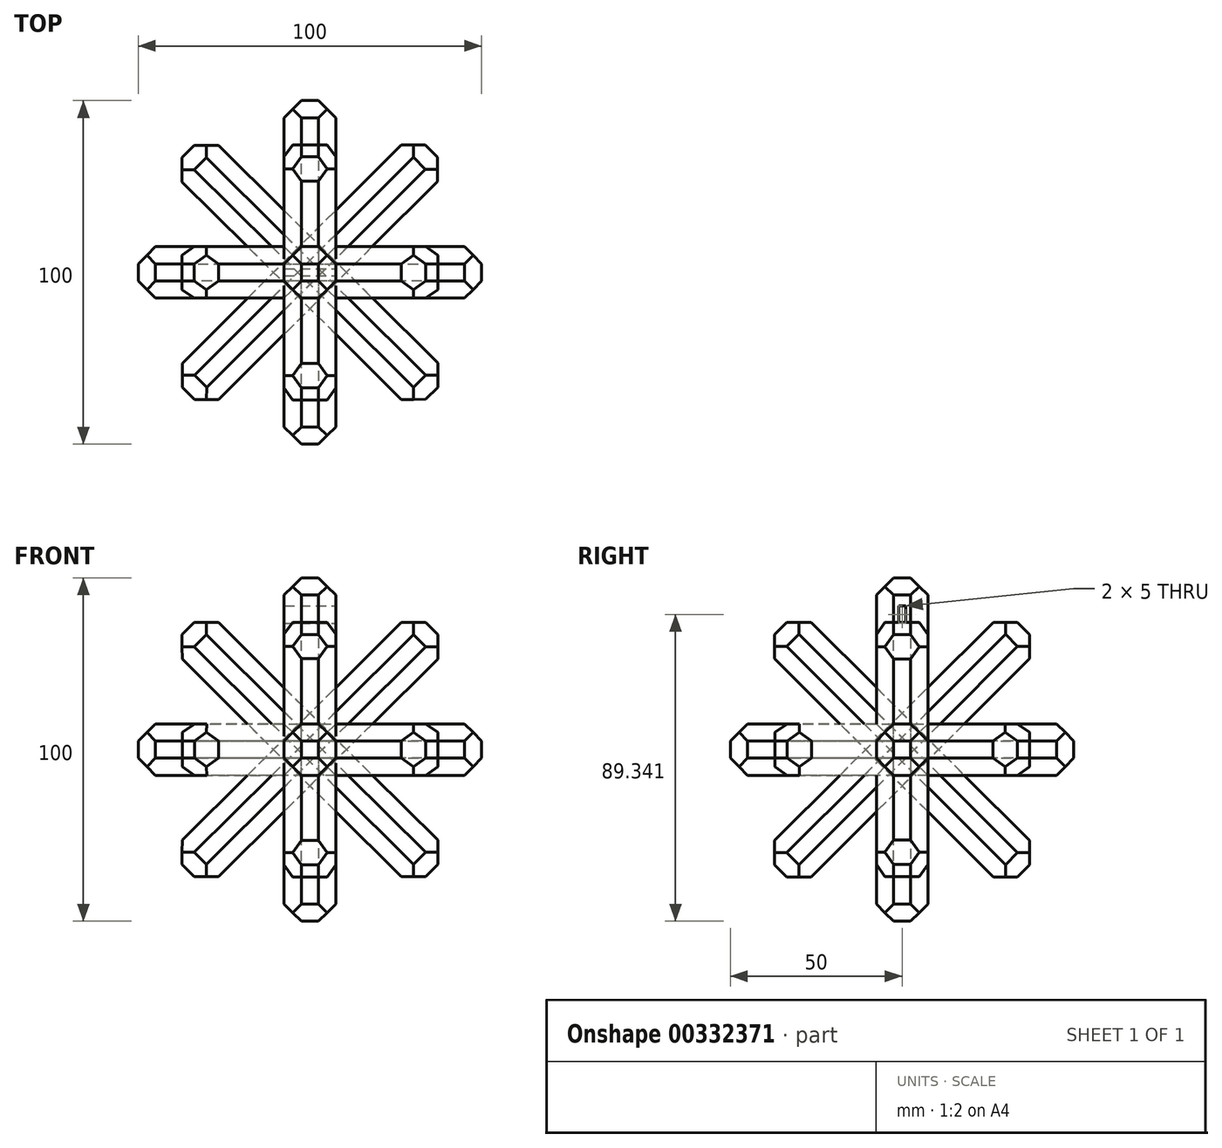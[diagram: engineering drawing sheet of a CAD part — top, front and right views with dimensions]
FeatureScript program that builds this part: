
annotation { "Feature Type Name" : "Feature", "Feature Type Description" : "" }
export const myFeature = defineFeature(function(context is Context, id is Id, definition is map)
    precondition{}
    {
        {
            var Q0;
            Q0=qCreatedBy(makeId("Top.planeOp"),FACE);
            var sketch = newSketch(context, id + "F0", { "sketchPlane" : qUnion([Q0])});
            skLineSegment(sketch, "E0.bottom", {"start": v(50, 7.5) * mm, "end": v(-50, 7.5) * mm});
            skLineSegment(sketch, "E0.top", {"start": v(50, -7.5) * mm, "end": v(-50, -7.5) * mm});
            skLineSegment(sketch, "E0.left", {"start": v(50, 7.5) * mm, "end": v(50, -7.5) * mm});
            skLineSegment(sketch, "E0.right", {"start": v(-50, 7.5) * mm, "end": v(-50, -7.5) * mm});
            skPoint(sketch, "E0.middle", {"position": v(0, 0) * mm});
            skSolve(sketch);
        }
        {
            var Q0;
            Q0=qCreatedBy(makeId("Right.planeOp"),FACE);
            var sketch = newSketch(context, id + "F1", { "sketchPlane" : qUnion([Q0])});
            skLineSegment(sketch, "E1.bottom", {"start": v(50, 7.5) * mm, "end": v(-50, 7.5) * mm});
            skLineSegment(sketch, "E1.top", {"start": v(50, -7.5) * mm, "end": v(-50, -7.5) * mm});
            skLineSegment(sketch, "E1.left", {"start": v(50, 7.5) * mm, "end": v(50, -7.5) * mm});
            skLineSegment(sketch, "E1.right", {"start": v(-50, 7.5) * mm, "end": v(-50, -7.5) * mm});
            skPoint(sketch, "E1.middle", {"position": v(0, 0) * mm});
            skSolve(sketch);
        }
        {
            var Q0;
            Q0 = qSketchRegion(id + "F0", true);
            extrude(context, id + "F2", {"entities" : qUnion([Q0]), "endBound" : BoundingType.SYMMETRIC, "depth" : 15 * mm});
        }
        {
            var Q0;
            Q0=makeQuery(id+"F1.imprint","IMPRINT",FACE,{"disambiguationData":[TD([[makeQuery(id+"F1.imprint","IMPRINT",EDGE,{"derivedFrom":sQuery(id+"F1.wireOp",EDGE,"E1.bottom")}),1.0]])]});
            extrude(context, id + "F3", {"entities" : qUnion([Q0]), "operationType" : NewBodyOperationType.ADD, "endBound" : BoundingType.SYMMETRIC, "depth" : 15 * mm});
        }
        {
            var Q0;
            Q0=qCreatedBy(makeId("Front.planeOp"),FACE);
            var sketch = newSketch(context, id + "F4", { "sketchPlane" : qUnion([Q0])});
            skLineSegment(sketch, "E2.bottom", {"start": v(-7.5, 50) * mm, "end": v(7.5, 50) * mm});
            skLineSegment(sketch, "E2.top", {"start": v(-7.5, -50) * mm, "end": v(7.5, -50) * mm});
            skLineSegment(sketch, "E2.left", {"start": v(-7.5, 50) * mm, "end": v(-7.5, -50) * mm});
            skLineSegment(sketch, "E2.right", {"start": v(7.5, 50) * mm, "end": v(7.5, -50) * mm});
            skPoint(sketch, "E2.middle", {"position": v(0, 0) * mm});
            skSolve(sketch);
        }
        {
            var Q0;
            Q0=makeQuery(id+"F4.imprint","IMPRINT",FACE,{"disambiguationData":[TD([[makeQuery(id+"F4.imprint","IMPRINT",EDGE,{"derivedFrom":sQuery(id+"F4.wireOp",EDGE,"E2.bottom")}),-1.0]])]});
            extrude(context, id + "F5", {"entities" : qUnion([Q0]), "operationType" : NewBodyOperationType.ADD, "endBound" : BoundingType.SYMMETRIC, "depth" : 15 * mm});
        }
        {
            var Q0;
            Q0=qCreatedBy(makeId("Top.planeOp"),FACE);
            var sketch = newSketch(context, id + "F6", { "sketchPlane" : qUnion([Q0])});
            skLineSegment(sketch, "E3.bottom", {"start": v(40.78, -29.9) * mm, "end": v(-30.21, 40.54) * mm});
            skLineSegment(sketch, "E3.top", {"start": v(30.21, -40.54) * mm, "end": v(-40.78, 29.9) * mm});
            skLineSegment(sketch, "E3.left", {"start": v(40.78, -29.9) * mm, "end": v(30.21, -40.54) * mm});
            skLineSegment(sketch, "E3.right", {"start": v(-30.21, 40.54) * mm, "end": v(-40.78, 29.9) * mm});
            skPoint(sketch, "E3.middle", {"position": v(0, 0) * mm});
            skSolve(sketch);
        }
        {
            var Q0;
            Q0=makeQuery(id+"F6.imprint","IMPRINT",FACE,{"disambiguationData":[TD([[makeQuery(id+"F6.imprint","IMPRINT",EDGE,{"derivedFrom":sQuery(id+"F6.wireOp",EDGE,"E3.bottom")}),1.0]])]});
            extrude(context, id + "F7", {"entities" : qUnion([Q0]), "endBound" : BoundingType.SYMMETRIC, "depth" : 15 * mm});
        }
        {
            var Q0;
            Q0=qCreatedBy(makeId("Top.planeOp"),FACE);
            var sketch = newSketch(context, id + "F8", { "sketchPlane" : qUnion([Q0])});
            skLineSegment(sketch, "E4.bottom", {"start": v(30.1, 40.62) * mm, "end": v(-40.7, -30) * mm});
            skLineSegment(sketch, "E4.top", {"start": v(40.7, 30) * mm, "end": v(-30.1, -40.62) * mm});
            skLineSegment(sketch, "E4.left", {"start": v(30.1, 40.62) * mm, "end": v(40.7, 30) * mm});
            skLineSegment(sketch, "E4.right", {"start": v(-40.7, -30) * mm, "end": v(-30.1, -40.62) * mm});
            skPoint(sketch, "E4.middle", {"position": v(0, 0) * mm});
            skSolve(sketch);
        }
        {
            var Q0;
            Q0=makeQuery(id+"F8.imprint","IMPRINT",FACE,{"disambiguationData":[TD([[makeQuery(id+"F8.imprint","IMPRINT",EDGE,{"derivedFrom":sQuery(id+"F8.wireOp",EDGE,"E4.bottom")}),1.0]])]});
            extrude(context, id + "F9", {"entities" : qUnion([Q0]), "endBound" : BoundingType.SYMMETRIC, "depth" : 15 * mm});
        }
        {
            var Q0;
            Q0=qCreatedBy(makeId("Front.planeOp"),FACE);
            var sketch = newSketch(context, id + "F10", { "sketchPlane" : qUnion([Q0])});
            skLineSegment(sketch, "E5.bottom", {"start": v(40.76, -29.9) * mm, "end": v(-30.2, 40.55) * mm});
            skLineSegment(sketch, "E5.top", {"start": v(30.2, -40.55) * mm, "end": v(-40.76, 29.9) * mm});
            skLineSegment(sketch, "E5.left", {"start": v(40.76, -29.9) * mm, "end": v(30.2, -40.55) * mm});
            skLineSegment(sketch, "E5.right", {"start": v(-30.2, 40.55) * mm, "end": v(-40.76, 29.9) * mm});
            skPoint(sketch, "E5.middle", {"position": v(0, 0) * mm});
            skSolve(sketch);
        }
        {
            var Q0;
            Q0=makeQuery(id+"F10.imprint","IMPRINT",FACE,{"disambiguationData":[TD([[makeQuery(id+"F10.imprint","IMPRINT",EDGE,{"derivedFrom":sQuery(id+"F10.wireOp",EDGE,"E5.bottom")}),1.0]])]});
            extrude(context, id + "F11", {"entities" : qUnion([Q0]), "endBound" : BoundingType.SYMMETRIC, "depth" : 15 * mm});
        }
        {
            var Q0;
            Q0=makeQuery(id+"F11.opExtrude","SWEPT_BODY",BODY,{"disambiguationData":[OSD([sQuery(id+"F10.wireOp",EDGE,"E5.bottom"),sQuery(id+"F10.wireOp",EDGE,"E5.top"),sQuery(id+"F10.wireOp",EDGE,"E5.left"),sQuery(id+"F10.wireOp",EDGE,"E5.right")])]});
            var Q1;
            Q1=qCreatedBy(makeId("Right.planeOp"),FACE);
            mirror(context, id + "F12", {"entities" : qUnion([Q0]), "mirrorPlane" : qUnion([Q1])});
        }
        {
            var Q0;
            Q0=qCreatedBy(makeId("Right.planeOp"),FACE);
            var sketch = newSketch(context, id + "F13", { "sketchPlane" : qUnion([Q0])});
            skLineSegment(sketch, "E6.bottom", {"start": v(-30.1, 40.62) * mm, "end": v(40.7, -30) * mm});
            skLineSegment(sketch, "E6.top", {"start": v(-40.7, 30) * mm, "end": v(30.1, -40.62) * mm});
            skLineSegment(sketch, "E6.left", {"start": v(-30.1, 40.62) * mm, "end": v(-40.7, 30) * mm});
            skLineSegment(sketch, "E6.right", {"start": v(40.7, -30) * mm, "end": v(30.1, -40.62) * mm});
            skPoint(sketch, "E6.middle", {"position": v(0, 0) * mm});
            skSolve(sketch);
        }
        {
            var Q0;
            Q0=makeQuery(id+"F13.imprint","IMPRINT",FACE,{"disambiguationData":[TD([[makeQuery(id+"F13.imprint","IMPRINT",EDGE,{"derivedFrom":sQuery(id+"F13.wireOp",EDGE,"E6.bottom")}),-1.0]])]});
            extrude(context, id + "F14", {"entities" : qUnion([Q0]), "endBound" : BoundingType.SYMMETRIC, "depth" : 15 * mm});
        }
        {
            var Q0;
            Q0=makeQuery(id+"F14.opExtrude","SWEPT_BODY",BODY,{"disambiguationData":[OSD([sQuery(id+"F13.wireOp",EDGE,"E6.bottom"),sQuery(id+"F13.wireOp",EDGE,"E6.top"),sQuery(id+"F13.wireOp",EDGE,"E6.left"),sQuery(id+"F13.wireOp",EDGE,"E6.right")])]});
            var Q1;
            Q1=qCreatedBy(makeId("Front.planeOp"),FACE);
            mirror(context, id + "F15", {"entities" : qUnion([Q0]), "mirrorPlane" : qUnion([Q1])});
        }
        {
            var Q0;
            Q0=makeQuery(id+"F14.opExtrude","SWEPT_EDGE",EDGE,{"disambiguationData":[OSD([sQuery(id+"F13.wireOp",EDGE,"E6.top"),sQuery(id+"F13.wireOp",EDGE,"E6.left")])]});
            chamfer(context, id + "F16", {"entities" : qUnion([Q0]), "width" : 5 * mm, "tangentPropagation" : true});
        }
        {
            var Q0;
            Q0=makeQuery(id+"F14.opExtrude","CAP_EDGE",EDGE,{"disambiguationData":[OSD([sQuery(id+"F13.wireOp",EDGE,"E6.left")])],"isStart":false});
            chamfer(context, id + "F17", {"entities" : qUnion([Q0]), "width" : 5 * mm, "tangentPropagation" : true});
        }
        {
            var Q0;
            Q0=makeQuery(id+"F14.opExtrude","SWEPT_EDGE",EDGE,{"disambiguationData":[OSD([sQuery(id+"F13.wireOp",EDGE,"E6.bottom"),sQuery(id+"F13.wireOp",EDGE,"E6.left")])]});
            chamfer(context, id + "F18", {"entities" : qUnion([Q0]), "width" : 5 * mm, "tangentPropagation" : true});
        }
        {
            var Q0;
            Q0=makeQuery(id+"F14.opExtrude","CAP_EDGE",EDGE,{"disambiguationData":[OSD([sQuery(id+"F13.wireOp",EDGE,"E6.left")])],"isStart":true});
            chamfer(context, id + "F19", {"entities" : qUnion([Q0]), "width" : 5 * mm, "tangentPropagation" : true});
        }
        {
            var Q0;
            Q0=makeQuery(id+"F3.opExtrude","SWEPT_EDGE",EDGE,{"disambiguationData":[OSD([sQuery(id+"F1.wireOp",EDGE,"E1.bottom"),sQuery(id+"F1.wireOp",EDGE,"E1.right")])]});
            chamfer(context, id + "F20", {"entities" : qUnion([Q0]), "width" : 5 * mm, "tangentPropagation" : true});
        }
        {
            var Q0;
            Q0=makeQuery(id+"F3.opExtrude","CAP_EDGE",EDGE,{"disambiguationData":[OSD([sQuery(id+"F1.wireOp",EDGE,"E1.right")])],"isStart":false});
            chamfer(context, id + "F21", {"entities" : qUnion([Q0]), "width" : 5 * mm, "tangentPropagation" : true});
        }
        {
            var Q0;
            Q0=makeQuery(id+"F3.opExtrude","CAP_EDGE",EDGE,{"disambiguationData":[OSD([sQuery(id+"F1.wireOp",EDGE,"E1.right")])],"isStart":true});
            chamfer(context, id + "F22", {"entities" : qUnion([Q0]), "width" : 5 * mm, "tangentPropagation" : true});
        }
        {
            var Q0;
            Q0=makeQuery(id+"F3.opExtrude","SWEPT_EDGE",EDGE,{"disambiguationData":[OSD([sQuery(id+"F1.wireOp",EDGE,"E1.top"),sQuery(id+"F1.wireOp",EDGE,"E1.right")])]});
            chamfer(context, id + "F23", {"entities" : qUnion([Q0]), "width" : 5 * mm, "tangentPropagation" : true});
        }
        {
            var Q0;
            {var subQ0=sQuery(id+"F1.wireOp",EDGE,"E1.bottom");var subQ2=sQuery(id+"F0.wireOp",EDGE,"E0.top");Q0=makeQuery(id+"F3.boolean.opBoolean","SPLIT",EDGE,{"disambiguationData":[TD([makeQuery(id+"F2.opExtrude","SWEPT_FACE",FACE,{"disambiguationData":[OSD([subQ2])]})])],"derivedFrom":makeQuery(id+"F3.opExtrude","CAP_EDGE",EDGE,{"disambiguationData":[OSD([subQ0])],"isStart":false})});}
            chamfer(context, id + "F24", {"entities" : qUnion([Q0]), "width" : 5 * mm, "tangentPropagation" : true});
        }
        {
            var Q0;
            {var subQ0=sQuery(id+"F1.wireOp",EDGE,"E1.bottom");var subQ1=sQuery(id+"F0.wireOp",EDGE,"E0.top");Q0=makeQuery(id+"F3.boolean.opBoolean","SPLIT",EDGE,{"disambiguationData":[TD([makeQuery(id+"F2.opExtrude","SWEPT_FACE",FACE,{"disambiguationData":[OSD([subQ1])]})])],"derivedFrom":makeQuery(id+"F3.opExtrude","CAP_EDGE",EDGE,{"disambiguationData":[OSD([subQ0])],"isStart":true})});}
            chamfer(context, id + "F25", {"entities" : qUnion([Q0]), "width" : 5 * mm, "tangentPropagation" : true});
        }
        {
            var Q0;
            {var subQ0=sQuery(id+"F1.wireOp",EDGE,"E1.top");var subQ2=sQuery(id+"F0.wireOp",EDGE,"E0.top");Q0=makeQuery(id+"F3.boolean.opBoolean","SPLIT",EDGE,{"disambiguationData":[TD([makeQuery(id+"F2.opExtrude","SWEPT_FACE",FACE,{"disambiguationData":[OSD([subQ2])]})])],"derivedFrom":makeQuery(id+"F3.opExtrude","CAP_EDGE",EDGE,{"disambiguationData":[OSD([subQ0])],"isStart":false})});}
            chamfer(context, id + "F26", {"entities" : qUnion([Q0]), "width" : 5 * mm, "tangentPropagation" : true});
        }
        {
            var Q0;
            {var subQ0=sQuery(id+"F1.wireOp",EDGE,"E1.top");var subQ2=sQuery(id+"F0.wireOp",EDGE,"E0.top");Q0=makeQuery(id+"F3.boolean.opBoolean","SPLIT",EDGE,{"disambiguationData":[TD([makeQuery(id+"F2.opExtrude","SWEPT_FACE",FACE,{"disambiguationData":[OSD([subQ2])]})])],"derivedFrom":makeQuery(id+"F3.opExtrude","CAP_EDGE",EDGE,{"disambiguationData":[OSD([subQ0])],"isStart":true})});}
            chamfer(context, id + "F27", {"entities" : qUnion([Q0]), "width" : 5 * mm, "tangentPropagation" : true});
        }
        {
            var Q0;
            Q0=makeQuery(id+"F5.opExtrude","SWEPT_EDGE",EDGE,{"disambiguationData":[OSD([sQuery(id+"F4.wireOp",EDGE,"E2.bottom"),sQuery(id+"F4.wireOp",EDGE,"E2.right")])]});
            chamfer(context, id + "F28", {"entities" : qUnion([Q0]), "width" : 5 * mm, "tangentPropagation" : true});
        }
        {
            var Q0;
            Q0=makeQuery(id+"F5.opExtrude","CAP_EDGE",EDGE,{"disambiguationData":[OSD([sQuery(id+"F4.wireOp",EDGE,"E2.bottom")])],"isStart":false});
            chamfer(context, id + "F29", {"entities" : qUnion([Q0]), "width" : 5 * mm, "tangentPropagation" : true});
        }
        {
            var Q0;
            Q0=makeQuery(id+"F5.opExtrude","CAP_EDGE",EDGE,{"disambiguationData":[OSD([sQuery(id+"F4.wireOp",EDGE,"E2.bottom")])],"isStart":true});
            chamfer(context, id + "F30", {"entities" : qUnion([Q0]), "width" : 5 * mm, "tangentPropagation" : true});
        }
        {
            var Q0;
            Q0=makeQuery(id+"F5.opExtrude","SWEPT_EDGE",EDGE,{"disambiguationData":[OSD([sQuery(id+"F4.wireOp",EDGE,"E2.bottom"),sQuery(id+"F4.wireOp",EDGE,"E2.left")])]});
            chamfer(context, id + "F31", {"entities" : qUnion([Q0]), "width" : 5 * mm, "tangentPropagation" : true});
        }
        {
            var Q0;
            {var subQ0=sQuery(id+"F1.wireOp",EDGE,"E1.bottom");var subQ2=sQuery(id+"F4.wireOp",EDGE,"E2.right");Q0=makeQuery(id+"F5.boolean.opBoolean","SPLIT",EDGE,{"disambiguationData":[TD([makeQuery(id+"F3.opExtrude","SWEPT_FACE",FACE,{"disambiguationData":[OSD([subQ0])]})])],"derivedFrom":makeQuery(id+"F5.opExtrude","CAP_EDGE",EDGE,{"disambiguationData":[OSD([subQ2])],"isStart":false})});}
            chamfer(context, id + "F32", {"entities" : qUnion([Q0]), "width" : 5 * mm, "tangentPropagation" : true});
        }
        {
            var Q0;
            {var subQ0=sQuery(id+"F1.wireOp",EDGE,"E1.bottom");var subQ2=sQuery(id+"F4.wireOp",EDGE,"E2.left");Q0=makeQuery(id+"F5.boolean.opBoolean","SPLIT",EDGE,{"disambiguationData":[TD([makeQuery(id+"F3.opExtrude","SWEPT_FACE",FACE,{"disambiguationData":[OSD([subQ0])]})])],"derivedFrom":makeQuery(id+"F5.opExtrude","CAP_EDGE",EDGE,{"disambiguationData":[OSD([subQ2])],"isStart":false})});}
            chamfer(context, id + "F33", {"entities" : qUnion([Q0]), "width" : 5 * mm, "tangentPropagation" : true});
        }
        {
            var Q0;
            {var subQ0=sQuery(id+"F1.wireOp",EDGE,"E1.bottom");var subQ3=sQuery(id+"F4.wireOp",EDGE,"E2.right");Q0=makeQuery(id+"F5.boolean.opBoolean","SPLIT",EDGE,{"disambiguationData":[TD([makeQuery(id+"F3.opExtrude","SWEPT_FACE",FACE,{"disambiguationData":[OSD([subQ0])]})])],"derivedFrom":makeQuery(id+"F5.opExtrude","CAP_EDGE",EDGE,{"disambiguationData":[OSD([subQ3])],"isStart":true})});}
            chamfer(context, id + "F34", {"entities" : qUnion([Q0]), "width" : 5 * mm, "tangentPropagation" : true});
        }
        {
            var Q0;
            {var subQ0=sQuery(id+"F1.wireOp",EDGE,"E1.bottom");var subQ2=sQuery(id+"F4.wireOp",EDGE,"E2.left");Q0=makeQuery(id+"F5.boolean.opBoolean","SPLIT",EDGE,{"disambiguationData":[TD([makeQuery(id+"F3.opExtrude","SWEPT_FACE",FACE,{"disambiguationData":[OSD([subQ0])]})])],"derivedFrom":makeQuery(id+"F5.opExtrude","CAP_EDGE",EDGE,{"disambiguationData":[OSD([subQ2])],"isStart":true})});}
            chamfer(context, id + "F35", {"entities" : qUnion([Q0]), "width" : 5 * mm, "tangentPropagation" : true});
        }
        {
            var Q0;
            Q0=makeQuery(id+"F5.opExtrude","SWEPT_EDGE",EDGE,{"disambiguationData":[OSD([sQuery(id+"F4.wireOp",EDGE,"E2.top"),sQuery(id+"F4.wireOp",EDGE,"E2.left")])]});
            chamfer(context, id + "F36", {"entities" : qUnion([Q0]), "width" : 5 * mm, "tangentPropagation" : true});
        }
        {
            var Q0;
            Q0=makeQuery(id+"F5.opExtrude","CAP_EDGE",EDGE,{"disambiguationData":[OSD([sQuery(id+"F4.wireOp",EDGE,"E2.top")])],"isStart":true});
            chamfer(context, id + "F37", {"entities" : qUnion([Q0]), "width" : 5 * mm, "tangentPropagation" : true});
        }
        {
            var Q0;
            Q0=makeQuery(id+"F5.opExtrude","CAP_EDGE",EDGE,{"disambiguationData":[OSD([sQuery(id+"F4.wireOp",EDGE,"E2.top")])],"isStart":false});
            chamfer(context, id + "F38", {"entities" : qUnion([Q0]), "width" : 5 * mm, "tangentPropagation" : true});
        }
        {
            var Q0;
            Q0=makeQuery(id+"F5.opExtrude","SWEPT_EDGE",EDGE,{"disambiguationData":[OSD([sQuery(id+"F4.wireOp",EDGE,"E2.top"),sQuery(id+"F4.wireOp",EDGE,"E2.right")])]});
            chamfer(context, id + "F39", {"entities" : qUnion([Q0]), "width" : 5 * mm, "tangentPropagation" : true});
        }
        {
            var Q0;
            {var subQ0=sQuery(id+"F1.wireOp",EDGE,"E1.top");var subQ3=sQuery(id+"F4.wireOp",EDGE,"E2.left");Q0=makeQuery(id+"F5.boolean.opBoolean","SPLIT",EDGE,{"disambiguationData":[TD([makeQuery(id+"F3.opExtrude","SWEPT_FACE",FACE,{"disambiguationData":[OSD([subQ0])]})])],"derivedFrom":makeQuery(id+"F5.opExtrude","CAP_EDGE",EDGE,{"disambiguationData":[OSD([subQ3])],"isStart":true})});}
            chamfer(context, id + "F40", {"entities" : qUnion([Q0]), "width" : 5 * mm, "tangentPropagation" : true});
        }
        {
            var Q0;
            {var subQ0=sQuery(id+"F1.wireOp",EDGE,"E1.top");var subQ3=sQuery(id+"F4.wireOp",EDGE,"E2.right");Q0=makeQuery(id+"F5.boolean.opBoolean","SPLIT",EDGE,{"disambiguationData":[TD([makeQuery(id+"F3.opExtrude","SWEPT_FACE",FACE,{"disambiguationData":[OSD([subQ0])]})])],"derivedFrom":makeQuery(id+"F5.opExtrude","CAP_EDGE",EDGE,{"disambiguationData":[OSD([subQ3])],"isStart":true})});}
            chamfer(context, id + "F41", {"entities" : qUnion([Q0]), "width" : 5 * mm, "tangentPropagation" : true});
        }
        {
            var Q0;
            {var subQ0=sQuery(id+"F1.wireOp",EDGE,"E1.top");var subQ3=sQuery(id+"F4.wireOp",EDGE,"E2.left");Q0=makeQuery(id+"F5.boolean.opBoolean","SPLIT",EDGE,{"disambiguationData":[TD([makeQuery(id+"F3.opExtrude","SWEPT_FACE",FACE,{"disambiguationData":[OSD([subQ0])]})])],"derivedFrom":makeQuery(id+"F5.opExtrude","CAP_EDGE",EDGE,{"disambiguationData":[OSD([subQ3])],"isStart":false})});}
            chamfer(context, id + "F42", {"entities" : qUnion([Q0]), "width" : 5 * mm, "tangentPropagation" : true});
        }
        {
            var Q0;
            {var subQ0=sQuery(id+"F1.wireOp",EDGE,"E1.top");var subQ2=sQuery(id+"F4.wireOp",EDGE,"E2.right");Q0=makeQuery(id+"F5.boolean.opBoolean","SPLIT",EDGE,{"disambiguationData":[TD([makeQuery(id+"F3.opExtrude","SWEPT_FACE",FACE,{"disambiguationData":[OSD([subQ0])]})])],"derivedFrom":makeQuery(id+"F5.opExtrude","CAP_EDGE",EDGE,{"disambiguationData":[OSD([subQ2])],"isStart":false})});}
            chamfer(context, id + "F43", {"entities" : qUnion([Q0]), "width" : 5 * mm, "tangentPropagation" : true});
        }
        {
            var Q0;
            Q0=makeQuery(id+"F14.opExtrude","SWEPT_EDGE",EDGE,{"disambiguationData":[OSD([sQuery(id+"F13.wireOp",EDGE,"E6.top"),sQuery(id+"F13.wireOp",EDGE,"E6.right")])]});
            chamfer(context, id + "F44", {"entities" : qUnion([Q0]), "width" : 5 * mm, "tangentPropagation" : true});
        }
        {
            var Q0;
            Q0=makeQuery(id+"F14.opExtrude","CAP_EDGE",EDGE,{"disambiguationData":[OSD([sQuery(id+"F13.wireOp",EDGE,"E6.right")])],"isStart":false});
            chamfer(context, id + "F45", {"entities" : qUnion([Q0]), "width" : 5 * mm, "tangentPropagation" : true});
        }
        {
            var Q0;
            Q0=makeQuery(id+"F14.opExtrude","CAP_EDGE",EDGE,{"disambiguationData":[OSD([sQuery(id+"F13.wireOp",EDGE,"E6.right")])],"isStart":true});
            chamfer(context, id + "F46", {"entities" : qUnion([Q0]), "width" : 5 * mm, "tangentPropagation" : true});
        }
        {
            var Q0;
            Q0=makeQuery(id+"F14.opExtrude","SWEPT_EDGE",EDGE,{"disambiguationData":[OSD([sQuery(id+"F13.wireOp",EDGE,"E6.bottom"),sQuery(id+"F13.wireOp",EDGE,"E6.right")])]});
            chamfer(context, id + "F47", {"entities" : qUnion([Q0]), "width" : 5 * mm, "tangentPropagation" : true});
        }
        {
            var Q0;
            Q0=makeQuery(id+"F14.opExtrude","CAP_EDGE",EDGE,{"disambiguationData":[OSD([sQuery(id+"F13.wireOp",EDGE,"E6.bottom")])],"isStart":true});
            chamfer(context, id + "F48", {"entities" : qUnion([Q0]), "width" : 5 * mm, "tangentPropagation" : true});
        }
        {
            var Q0;
            Q0=makeQuery(id+"F14.opExtrude","CAP_EDGE",EDGE,{"disambiguationData":[OSD([sQuery(id+"F13.wireOp",EDGE,"E6.top")])],"isStart":true});
            chamfer(context, id + "F49", {"entities" : qUnion([Q0]), "width" : 5 * mm, "tangentPropagation" : true});
        }
        {
            var Q0;
            Q0=makeQuery(id+"F14.opExtrude","CAP_EDGE",EDGE,{"disambiguationData":[OSD([sQuery(id+"F13.wireOp",EDGE,"E6.bottom")])],"isStart":false});
            chamfer(context, id + "F50", {"entities" : qUnion([Q0]), "width" : 5 * mm, "tangentPropagation" : true});
        }
        {
            var Q0;
            Q0=makeQuery(id+"F14.opExtrude","CAP_EDGE",EDGE,{"disambiguationData":[OSD([sQuery(id+"F13.wireOp",EDGE,"E6.top")])],"isStart":false});
            chamfer(context, id + "F51", {"entities" : qUnion([Q0]), "width" : 5 * mm, "tangentPropagation" : true});
        }
        {
            var Q0;
            Q0=makeQuery(id+"F15.opPattern","COPY",EDGE,{"derivedFrom":makeQuery(id+"F14.opExtrude","SWEPT_EDGE",EDGE,{"disambiguationData":[OSD([sQuery(id+"F13.wireOp",EDGE,"E6.bottom"),sQuery(id+"F13.wireOp",EDGE,"E6.left")])]}),"instanceName":"1"});
            chamfer(context, id + "F52", {"entities" : qUnion([Q0]), "width" : 5 * mm, "tangentPropagation" : true});
        }
        {
            var Q0;
            Q0=makeQuery(id+"F15.opPattern","COPY",EDGE,{"derivedFrom":makeQuery(id+"F14.opExtrude","SWEPT_EDGE",EDGE,{"disambiguationData":[OSD([sQuery(id+"F13.wireOp",EDGE,"E6.top"),sQuery(id+"F13.wireOp",EDGE,"E6.left")])]}),"instanceName":"1"});
            chamfer(context, id + "F53", {"entities" : qUnion([Q0]), "width" : 5 * mm, "tangentPropagation" : true});
        }
        {
            var Q0;
            Q0=makeQuery(id+"F15.opPattern","COPY",EDGE,{"derivedFrom":makeQuery(id+"F14.opExtrude","CAP_EDGE",EDGE,{"disambiguationData":[OSD([sQuery(id+"F13.wireOp",EDGE,"E6.left")])],"isStart":false}),"instanceName":"1"});
            chamfer(context, id + "F54", {"entities" : qUnion([Q0]), "width" : 5 * mm, "tangentPropagation" : true});
        }
        {
            var Q0;
            Q0=makeQuery(id+"F15.opPattern","COPY",EDGE,{"derivedFrom":makeQuery(id+"F14.opExtrude","CAP_EDGE",EDGE,{"disambiguationData":[OSD([sQuery(id+"F13.wireOp",EDGE,"E6.left")])],"isStart":true}),"instanceName":"1"});
            chamfer(context, id + "F55", {"entities" : qUnion([Q0]), "width" : 5 * mm, "tangentPropagation" : true});
        }
        {
            var Q0;
            Q0=makeQuery(id+"F15.opPattern","COPY",EDGE,{"derivedFrom":makeQuery(id+"F14.opExtrude","CAP_EDGE",EDGE,{"disambiguationData":[OSD([sQuery(id+"F13.wireOp",EDGE,"E6.right")])],"isStart":false}),"instanceName":"1"});
            chamfer(context, id + "F56", {"entities" : qUnion([Q0]), "width" : 5 * mm, "tangentPropagation" : true});
        }
        {
            var Q0;
            Q0=makeQuery(id+"F15.opPattern","COPY",EDGE,{"derivedFrom":makeQuery(id+"F14.opExtrude","SWEPT_EDGE",EDGE,{"disambiguationData":[OSD([sQuery(id+"F13.wireOp",EDGE,"E6.top"),sQuery(id+"F13.wireOp",EDGE,"E6.right")])]}),"instanceName":"1"});
            chamfer(context, id + "F57", {"entities" : qUnion([Q0]), "width" : 5 * mm, "tangentPropagation" : true});
        }
        {
            var Q0;
            Q0=makeQuery(id+"F15.opPattern","COPY",EDGE,{"derivedFrom":makeQuery(id+"F14.opExtrude","SWEPT_EDGE",EDGE,{"disambiguationData":[OSD([sQuery(id+"F13.wireOp",EDGE,"E6.bottom"),sQuery(id+"F13.wireOp",EDGE,"E6.right")])]}),"instanceName":"1"});
            chamfer(context, id + "F58", {"entities" : qUnion([Q0]), "width" : 5 * mm, "tangentPropagation" : true});
        }
        {
            var Q0;
            Q0=makeQuery(id+"F15.opPattern","COPY",EDGE,{"derivedFrom":makeQuery(id+"F14.opExtrude","CAP_EDGE",EDGE,{"disambiguationData":[OSD([sQuery(id+"F13.wireOp",EDGE,"E6.right")])],"isStart":true}),"instanceName":"1"});
            chamfer(context, id + "F59", {"entities" : qUnion([Q0]), "width" : 5 * mm, "tangentPropagation" : true});
        }
        {
            var Q0;
            Q0=makeQuery(id+"F15.opPattern","COPY",EDGE,{"derivedFrom":makeQuery(id+"F14.opExtrude","CAP_EDGE",EDGE,{"disambiguationData":[OSD([sQuery(id+"F13.wireOp",EDGE,"E6.bottom")])],"isStart":false}),"instanceName":"1"});
            chamfer(context, id + "F60", {"entities" : qUnion([Q0]), "width" : 5 * mm, "tangentPropagation" : true});
        }
        {
            var Q0;
            Q0=makeQuery(id+"F15.opPattern","COPY",EDGE,{"derivedFrom":makeQuery(id+"F14.opExtrude","CAP_EDGE",EDGE,{"disambiguationData":[OSD([sQuery(id+"F13.wireOp",EDGE,"E6.top")])],"isStart":false}),"instanceName":"1"});
            chamfer(context, id + "F61", {"entities" : qUnion([Q0]), "width" : 5 * mm, "tangentPropagation" : true});
        }
        {
            var Q0;
            Q0=makeQuery(id+"F15.opPattern","COPY",EDGE,{"derivedFrom":makeQuery(id+"F14.opExtrude","CAP_EDGE",EDGE,{"disambiguationData":[OSD([sQuery(id+"F13.wireOp",EDGE,"E6.bottom")])],"isStart":true}),"instanceName":"1"});
            chamfer(context, id + "F62", {"entities" : qUnion([Q0]), "width" : 5 * mm, "tangentPropagation" : true});
        }
        {
            var Q0;
            Q0=makeQuery(id+"F15.opPattern","COPY",EDGE,{"derivedFrom":makeQuery(id+"F14.opExtrude","CAP_EDGE",EDGE,{"disambiguationData":[OSD([sQuery(id+"F13.wireOp",EDGE,"E6.top")])],"isStart":true}),"instanceName":"1"});
            chamfer(context, id + "F63", {"entities" : qUnion([Q0]), "width" : 5 * mm, "tangentPropagation" : true});
        }
        {
            var Q0;
            Q0=makeQuery(id+"F11.opExtrude","SWEPT_FACE",FACE,{"disambiguationData":[OSD([sQuery(id+"F10.wireOp",EDGE,"E5.right")])]});
            chamfer(context, id + "F64", {"entities" : qUnion([Q0]), "width" : 5 * mm, "tangentPropagation" : true});
        }
        {
            var Q0;
            Q0=makeQuery(id+"F2.opExtrude","SWEPT_FACE",FACE,{"disambiguationData":[OSD([sQuery(id+"F0.wireOp",EDGE,"E0.right")])]});
            chamfer(context, id + "F65", {"entities" : qUnion([Q0]), "width" : 5 * mm, "tangentPropagation" : true});
        }
        {
            var Q0;
            Q0=makeQuery(id+"F9.opExtrude","SWEPT_FACE",FACE,{"disambiguationData":[OSD([sQuery(id+"F8.wireOp",EDGE,"E4.right")])]});
            chamfer(context, id + "F66", {"entities" : qUnion([Q0]), "width" : 5 * mm, "tangentPropagation" : true});
        }
        {
            var Q0;
            Q0=makeQuery(id+"F7.opExtrude","SWEPT_FACE",FACE,{"disambiguationData":[OSD([sQuery(id+"F6.wireOp",EDGE,"E3.right")])]});
            chamfer(context, id + "F67", {"entities" : qUnion([Q0]), "width" : 5 * mm, "tangentPropagation" : true});
        }
        {
            var Q0;
            Q0=makeQuery(id+"F7.opExtrude","SWEPT_FACE",FACE,{"disambiguationData":[OSD([sQuery(id+"F6.wireOp",EDGE,"E3.left")])]});
            chamfer(context, id + "F68", {"entities" : qUnion([Q0]), "width" : 5 * mm, "tangentPropagation" : true});
        }
        {
            var Q0;
            Q0=makeQuery(id+"F2.opExtrude","SWEPT_FACE",FACE,{"disambiguationData":[OSD([sQuery(id+"F0.wireOp",EDGE,"E0.left")])]});
            chamfer(context, id + "F69", {"entities" : qUnion([Q0]), "width" : 5 * mm, "tangentPropagation" : true});
        }
        {
            var Q0;
            Q0=makeQuery(id+"F12.opPattern","COPY",FACE,{"derivedFrom":makeQuery(id+"F11.opExtrude","SWEPT_FACE",FACE,{"disambiguationData":[OSD([sQuery(id+"F10.wireOp",EDGE,"E5.right")])]}),"instanceName":"1"});
            chamfer(context, id + "F70", {"entities" : qUnion([Q0]), "width" : 5 * mm, "tangentPropagation" : true});
        }
        {
            var Q0;
            Q0=makeQuery(id+"F9.opExtrude","SWEPT_FACE",FACE,{"disambiguationData":[OSD([sQuery(id+"F8.wireOp",EDGE,"E4.left")])]});
            chamfer(context, id + "F71", {"entities" : qUnion([Q0]), "width" : 5 * mm, "tangentPropagation" : true});
        }
        {
            var Q0;
            Q0=makeQuery(id+"F3.opExtrude","SWEPT_FACE",FACE,{"disambiguationData":[OSD([sQuery(id+"F1.wireOp",EDGE,"E1.left")])]});
            chamfer(context, id + "F72", {"entities" : qUnion([Q0]), "width" : 5 * mm, "tangentPropagation" : true});
        }
        {
            var Q0;
            Q0=makeQuery(id+"F11.opExtrude","SWEPT_FACE",FACE,{"disambiguationData":[OSD([sQuery(id+"F10.wireOp",EDGE,"E5.left")])]});
            chamfer(context, id + "F73", {"entities" : qUnion([Q0]), "width" : 5 * mm, "tangentPropagation" : true});
        }
        {
            var Q0;
            {var subQ1=sQuery(id+"F0.wireOp",EDGE,"E0.left");var subQ2=sQuery(id+"F0.wireOp",EDGE,"E0.bottom");Q0=makeQuery(id+"F3.boolean.opBoolean","SPLIT",EDGE,{"disambiguationData":[TD([makeQuery(id+"F2.opExtrude","SWEPT_FACE",FACE,{"disambiguationData":[OSD([subQ1])]})])],"derivedFrom":makeQuery(id+"F2.opExtrude","CAP_EDGE",EDGE,{"disambiguationData":[OSD([subQ2])],"isStart":false})});}
            chamfer(context, id + "F74", {"entities" : qUnion([Q0]), "width" : 5 * mm, "tangentPropagation" : true});
        }
        {
            var Q0;
            {var subQ1=sQuery(id+"F0.wireOp",EDGE,"E0.left");var subQ2=sQuery(id+"F0.wireOp",EDGE,"E0.top");Q0=makeQuery(id+"F3.boolean.opBoolean","SPLIT",EDGE,{"disambiguationData":[TD([makeQuery(id+"F2.opExtrude","SWEPT_FACE",FACE,{"disambiguationData":[OSD([subQ1])]})])],"derivedFrom":makeQuery(id+"F2.opExtrude","CAP_EDGE",EDGE,{"disambiguationData":[OSD([subQ2])],"isStart":false})});}
            chamfer(context, id + "F75", {"entities" : qUnion([Q0]), "width" : 5 * mm, "tangentPropagation" : true});
        }
        {
            var Q0;
            Q0=makeQuery(id+"F11.opExtrude","CAP_EDGE",EDGE,{"disambiguationData":[OSD([sQuery(id+"F10.wireOp",EDGE,"E5.bottom")])],"isStart":true});
            chamfer(context, id + "F76", {"entities" : qUnion([Q0]), "width" : 5 * mm, "tangentPropagation" : true});
        }
        {
            var Q0;
            Q0=makeQuery(id+"F11.opExtrude","CAP_EDGE",EDGE,{"disambiguationData":[OSD([sQuery(id+"F10.wireOp",EDGE,"E5.bottom")])],"isStart":false});
            chamfer(context, id + "F77", {"entities" : qUnion([Q0]), "width" : 5 * mm, "tangentPropagation" : true});
        }
        {
            var Q0;
            {var subQ1=sQuery(id+"F0.wireOp",EDGE,"E0.left");var subQ2=sQuery(id+"F0.wireOp",EDGE,"E0.bottom");Q0=makeQuery(id+"F3.boolean.opBoolean","SPLIT",EDGE,{"disambiguationData":[TD([makeQuery(id+"F2.opExtrude","SWEPT_FACE",FACE,{"disambiguationData":[OSD([subQ1])]})])],"derivedFrom":makeQuery(id+"F2.opExtrude","CAP_EDGE",EDGE,{"disambiguationData":[OSD([subQ2])],"isStart":true})});}
            chamfer(context, id + "F78", {"entities" : qUnion([Q0]), "width" : 5 * mm, "tangentPropagation" : true});
        }
        {
            var Q0;
            {var subQ0=sQuery(id+"F0.wireOp",EDGE,"E0.left");var subQ2=sQuery(id+"F0.wireOp",EDGE,"E0.top");Q0=makeQuery(id+"F3.boolean.opBoolean","SPLIT",EDGE,{"disambiguationData":[TD([makeQuery(id+"F2.opExtrude","SWEPT_FACE",FACE,{"disambiguationData":[OSD([subQ0])]})])],"derivedFrom":makeQuery(id+"F2.opExtrude","CAP_EDGE",EDGE,{"disambiguationData":[OSD([subQ2])],"isStart":true})});}
            chamfer(context, id + "F79", {"entities" : qUnion([Q0]), "width" : 5 * mm, "tangentPropagation" : true});
        }
        {
            var Q0;
            Q0=makeQuery(id+"F7.opExtrude","CAP_EDGE",EDGE,{"disambiguationData":[OSD([sQuery(id+"F6.wireOp",EDGE,"E3.bottom")])],"isStart":false});
            chamfer(context, id + "F80", {"entities" : qUnion([Q0]), "width" : 5 * mm, "tangentPropagation" : true});
        }
        {
            var Q0;
            Q0=makeQuery(id+"F7.opExtrude","CAP_EDGE",EDGE,{"disambiguationData":[OSD([sQuery(id+"F6.wireOp",EDGE,"E3.top")])],"isStart":false});
            chamfer(context, id + "F81", {"entities" : qUnion([Q0]), "width" : 5 * mm, "tangentPropagation" : true});
        }
        {
            var Q0;
            Q0=makeQuery(id+"F7.opExtrude","CAP_EDGE",EDGE,{"disambiguationData":[OSD([sQuery(id+"F6.wireOp",EDGE,"E3.top")])],"isStart":true});
            chamfer(context, id + "F82", {"entities" : qUnion([Q0]), "width" : 5 * mm, "tangentPropagation" : true});
        }
        {
            var Q0;
            Q0=makeQuery(id+"F7.opExtrude","CAP_EDGE",EDGE,{"disambiguationData":[OSD([sQuery(id+"F6.wireOp",EDGE,"E3.bottom")])],"isStart":true});
            chamfer(context, id + "F83", {"entities" : qUnion([Q0]), "width" : 5 * mm, "tangentPropagation" : true});
        }
        {
            var Q0;
            Q0=makeQuery(id+"F11.opExtrude","CAP_EDGE",EDGE,{"disambiguationData":[OSD([sQuery(id+"F10.wireOp",EDGE,"E5.top")])],"isStart":false});
            chamfer(context, id + "F84", {"entities" : qUnion([Q0]), "width" : 5 * mm, "tangentPropagation" : true});
        }
        {
            var Q0;
            Q0=makeQuery(id+"F11.opExtrude","CAP_EDGE",EDGE,{"disambiguationData":[OSD([sQuery(id+"F10.wireOp",EDGE,"E5.top")])],"isStart":true});
            chamfer(context, id + "F85", {"entities" : qUnion([Q0]), "width" : 5 * mm, "tangentPropagation" : true});
        }
        {
            var Q0;
            Q0=makeQuery(id+"F9.opExtrude","CAP_EDGE",EDGE,{"disambiguationData":[OSD([sQuery(id+"F8.wireOp",EDGE,"E4.top")])],"isStart":true});
            chamfer(context, id + "F86", {"entities" : qUnion([Q0]), "width" : 5 * mm, "tangentPropagation" : true});
        }
        {
            var Q0;
            Q0=makeQuery(id+"F9.opExtrude","CAP_EDGE",EDGE,{"disambiguationData":[OSD([sQuery(id+"F8.wireOp",EDGE,"E4.bottom")])],"isStart":true});
            chamfer(context, id + "F87", {"entities" : qUnion([Q0]), "width" : 5 * mm, "tangentPropagation" : true});
        }
        {
            var Q0;
            Q0=makeQuery(id+"F9.opExtrude","CAP_EDGE",EDGE,{"disambiguationData":[OSD([sQuery(id+"F8.wireOp",EDGE,"E4.top")])],"isStart":false});
            chamfer(context, id + "F88", {"entities" : qUnion([Q0]), "width" : 5 * mm, "tangentPropagation" : true});
        }
        {
            var Q0;
            {var subQ0=sQuery(id+"F1.wireOp",EDGE,"E1.top");var subQ2=sQuery(id+"F0.wireOp",EDGE,"E0.bottom");Q0=makeQuery(id+"F3.boolean.opBoolean","SPLIT",EDGE,{"disambiguationData":[TD([makeQuery(id+"F2.opExtrude","SWEPT_FACE",FACE,{"disambiguationData":[OSD([subQ2])]})])],"derivedFrom":makeQuery(id+"F3.opExtrude","CAP_EDGE",EDGE,{"disambiguationData":[OSD([subQ0])],"isStart":false})});}
            chamfer(context, id + "F89", {"entities" : qUnion([Q0]), "width" : 5 * mm, "tangentPropagation" : true});
        }
        {
            var Q0;
            {var subQ1=sQuery(id+"F1.wireOp",EDGE,"E1.bottom");var subQ2=sQuery(id+"F0.wireOp",EDGE,"E0.bottom");Q0=makeQuery(id+"F3.boolean.opBoolean","SPLIT",EDGE,{"disambiguationData":[TD([makeQuery(id+"F2.opExtrude","SWEPT_FACE",FACE,{"disambiguationData":[OSD([subQ2])]})])],"derivedFrom":makeQuery(id+"F3.opExtrude","CAP_EDGE",EDGE,{"disambiguationData":[OSD([subQ1])],"isStart":false})});}
            chamfer(context, id + "F90", {"entities" : qUnion([Q0]), "width" : 5 * mm, "tangentPropagation" : true});
        }
        {
            var Q0;
            {var subQ0=sQuery(id+"F1.wireOp",EDGE,"E1.top");var subQ2=sQuery(id+"F0.wireOp",EDGE,"E0.bottom");Q0=makeQuery(id+"F3.boolean.opBoolean","SPLIT",EDGE,{"disambiguationData":[TD([makeQuery(id+"F2.opExtrude","SWEPT_FACE",FACE,{"disambiguationData":[OSD([subQ2])]})])],"derivedFrom":makeQuery(id+"F3.opExtrude","CAP_EDGE",EDGE,{"disambiguationData":[OSD([subQ0])],"isStart":true})});}
            chamfer(context, id + "F91", {"entities" : qUnion([Q0]), "width" : 5 * mm, "tangentPropagation" : true});
        }
        {
            var Q0;
            Q0=makeQuery(id+"F9.opExtrude","CAP_EDGE",EDGE,{"disambiguationData":[OSD([sQuery(id+"F8.wireOp",EDGE,"E4.bottom")])],"isStart":false});
            chamfer(context, id + "F92", {"entities" : qUnion([Q0]), "width" : 5 * mm, "tangentPropagation" : true});
        }
        {
            var Q0;
            {var subQ0=sQuery(id+"F1.wireOp",EDGE,"E1.bottom");var subQ2=sQuery(id+"F0.wireOp",EDGE,"E0.bottom");Q0=makeQuery(id+"F3.boolean.opBoolean","SPLIT",EDGE,{"disambiguationData":[TD([makeQuery(id+"F2.opExtrude","SWEPT_FACE",FACE,{"disambiguationData":[OSD([subQ2])]})])],"derivedFrom":makeQuery(id+"F3.opExtrude","CAP_EDGE",EDGE,{"disambiguationData":[OSD([subQ0])],"isStart":true})});}
            chamfer(context, id + "F93", {"entities" : qUnion([Q0]), "width" : 5 * mm, "tangentPropagation" : true});
        }
        {
            var Q0;
            {var subQ1=sQuery(id+"F0.wireOp",EDGE,"E0.right");var subQ2=sQuery(id+"F0.wireOp",EDGE,"E0.top");Q0=makeQuery(id+"F3.boolean.opBoolean","SPLIT",EDGE,{"disambiguationData":[TD([makeQuery(id+"F2.opExtrude","SWEPT_FACE",FACE,{"disambiguationData":[OSD([subQ1])]})])],"derivedFrom":makeQuery(id+"F2.opExtrude","CAP_EDGE",EDGE,{"disambiguationData":[OSD([subQ2])],"isStart":false})});}
            chamfer(context, id + "F94", {"entities" : qUnion([Q0]), "width" : 5 * mm, "tangentPropagation" : true});
        }
        {
            var Q0;
            {var subQ1=sQuery(id+"F0.wireOp",EDGE,"E0.right");var subQ2=sQuery(id+"F0.wireOp",EDGE,"E0.bottom");Q0=makeQuery(id+"F3.boolean.opBoolean","SPLIT",EDGE,{"disambiguationData":[TD([makeQuery(id+"F2.opExtrude","SWEPT_FACE",FACE,{"disambiguationData":[OSD([subQ1])]})])],"derivedFrom":makeQuery(id+"F2.opExtrude","CAP_EDGE",EDGE,{"disambiguationData":[OSD([subQ2])],"isStart":false})});}
            chamfer(context, id + "F95", {"entities" : qUnion([Q0]), "width" : 5 * mm, "tangentPropagation" : true});
        }
        {
            var Q0;
            {var subQ1=sQuery(id+"F0.wireOp",EDGE,"E0.right");var subQ2=sQuery(id+"F0.wireOp",EDGE,"E0.bottom");Q0=makeQuery(id+"F3.boolean.opBoolean","SPLIT",EDGE,{"disambiguationData":[TD([makeQuery(id+"F2.opExtrude","SWEPT_FACE",FACE,{"disambiguationData":[OSD([subQ1])]})])],"derivedFrom":makeQuery(id+"F2.opExtrude","CAP_EDGE",EDGE,{"disambiguationData":[OSD([subQ2])],"isStart":true})});}
            chamfer(context, id + "F96", {"entities" : qUnion([Q0]), "width" : 5 * mm, "tangentPropagation" : true});
        }
        {
            var Q0;
            Q0=makeQuery(id+"F12.opPattern","COPY",FACE,{"derivedFrom":makeQuery(id+"F11.opExtrude","SWEPT_FACE",FACE,{"disambiguationData":[OSD([sQuery(id+"F10.wireOp",EDGE,"E5.left")])]}),"instanceName":"1"});
            chamfer(context, id + "F97", {"entities" : qUnion([Q0]), "width" : 5 * mm, "tangentPropagation" : true});
        }
        {
            var Q0;
            Q0=makeQuery(id+"F12.opPattern","COPY",EDGE,{"derivedFrom":makeQuery(id+"F11.opExtrude","CAP_EDGE",EDGE,{"disambiguationData":[OSD([sQuery(id+"F10.wireOp",EDGE,"E5.bottom")])],"isStart":false}),"instanceName":"1"});
            chamfer(context, id + "F98", {"entities" : qUnion([Q0]), "width" : 5 * mm, "tangentPropagation" : true});
        }
        {
            var Q0;
            Q0=makeQuery(id+"F12.opPattern","COPY",EDGE,{"derivedFrom":makeQuery(id+"F11.opExtrude","CAP_EDGE",EDGE,{"disambiguationData":[OSD([sQuery(id+"F10.wireOp",EDGE,"E5.bottom")])],"isStart":true}),"instanceName":"1"});
            chamfer(context, id + "F99", {"entities" : qUnion([Q0]), "width" : 5 * mm, "tangentPropagation" : true});
        }
        {
            var Q0;
            Q0=makeQuery(id+"F12.opPattern","COPY",EDGE,{"derivedFrom":makeQuery(id+"F11.opExtrude","CAP_EDGE",EDGE,{"disambiguationData":[OSD([sQuery(id+"F10.wireOp",EDGE,"E5.top")])],"isStart":false}),"instanceName":"1"});
            chamfer(context, id + "F100", {"entities" : qUnion([Q0]), "width" : 5 * mm, "tangentPropagation" : true});
        }
        {
            var Q0;
            Q0=makeQuery(id+"F12.opPattern","COPY",EDGE,{"derivedFrom":makeQuery(id+"F11.opExtrude","CAP_EDGE",EDGE,{"disambiguationData":[OSD([sQuery(id+"F10.wireOp",EDGE,"E5.top")])],"isStart":true}),"instanceName":"1"});
            chamfer(context, id + "F101", {"entities" : qUnion([Q0]), "width" : 5 * mm, "tangentPropagation" : true});
        }
        {
            var Q0;
            {var subQ1=sQuery(id+"F0.wireOp",EDGE,"E0.right");var subQ2=sQuery(id+"F0.wireOp",EDGE,"E0.top");Q0=makeQuery(id+"F3.boolean.opBoolean","SPLIT",EDGE,{"disambiguationData":[TD([makeQuery(id+"F2.opExtrude","SWEPT_FACE",FACE,{"disambiguationData":[OSD([subQ1])]})])],"derivedFrom":makeQuery(id+"F2.opExtrude","CAP_EDGE",EDGE,{"disambiguationData":[OSD([subQ2])],"isStart":true})});}
            chamfer(context, id + "F102", {"entities" : qUnion([Q0]), "width" : 5 * mm, "tangentPropagation" : true});
        }
        {
            var Q0;
            {var subQ0=sQuery(id+"F1.wireOp",EDGE,"E1.bottom");var subQ3=sQuery(id+"F4.wireOp",EDGE,"E2.right");Q0=makeQuery(id+"F5.boolean.opBoolean","SPLIT",FACE,{"disambiguationData":[TD([makeQuery(id+"F3.opExtrude","SWEPT_FACE",FACE,{"disambiguationData":[OSD([subQ0])]})])],"derivedFrom":makeQuery(id+"F5.opExtrude","SWEPT_FACE",FACE,{"disambiguationData":[OSD([subQ3])]})});}
            var sketch = newSketch(context, id + "F103", { "sketchPlane" : qUnion([Q0])});
            skLineSegment(sketch, "E7.bottom", {"start": v(1, 41.84) * mm, "end": v(-1, 41.84) * mm});
            skLineSegment(sketch, "E7.top", {"start": v(1, 36.84) * mm, "end": v(-1, 36.84) * mm});
            skLineSegment(sketch, "E7.left", {"start": v(1, 41.84) * mm, "end": v(1, 36.84) * mm});
            skLineSegment(sketch, "E7.right", {"start": v(-1, 41.84) * mm, "end": v(-1, 36.84) * mm});
            skPoint(sketch, "E7.middle", {"position": v(0, 39.34) * mm});
            skSolve(sketch);
        }
        {
            var Q0;
            Q0=makeQuery(id+"F103.imprint","IMPRINT",FACE,{"disambiguationData":[TD([[makeQuery(id+"F103.imprint","IMPRINT",EDGE,{"derivedFrom":sQuery(id+"F103.wireOp",EDGE,"E7.bottom")}),1.0]])]});
            extrude(context, id + "F104", {"entities" : qUnion([Q0]), "operationType" : NewBodyOperationType.REMOVE, "oppositeDirection" : true, "depth" : 23.8 * mm});
        }
    });
